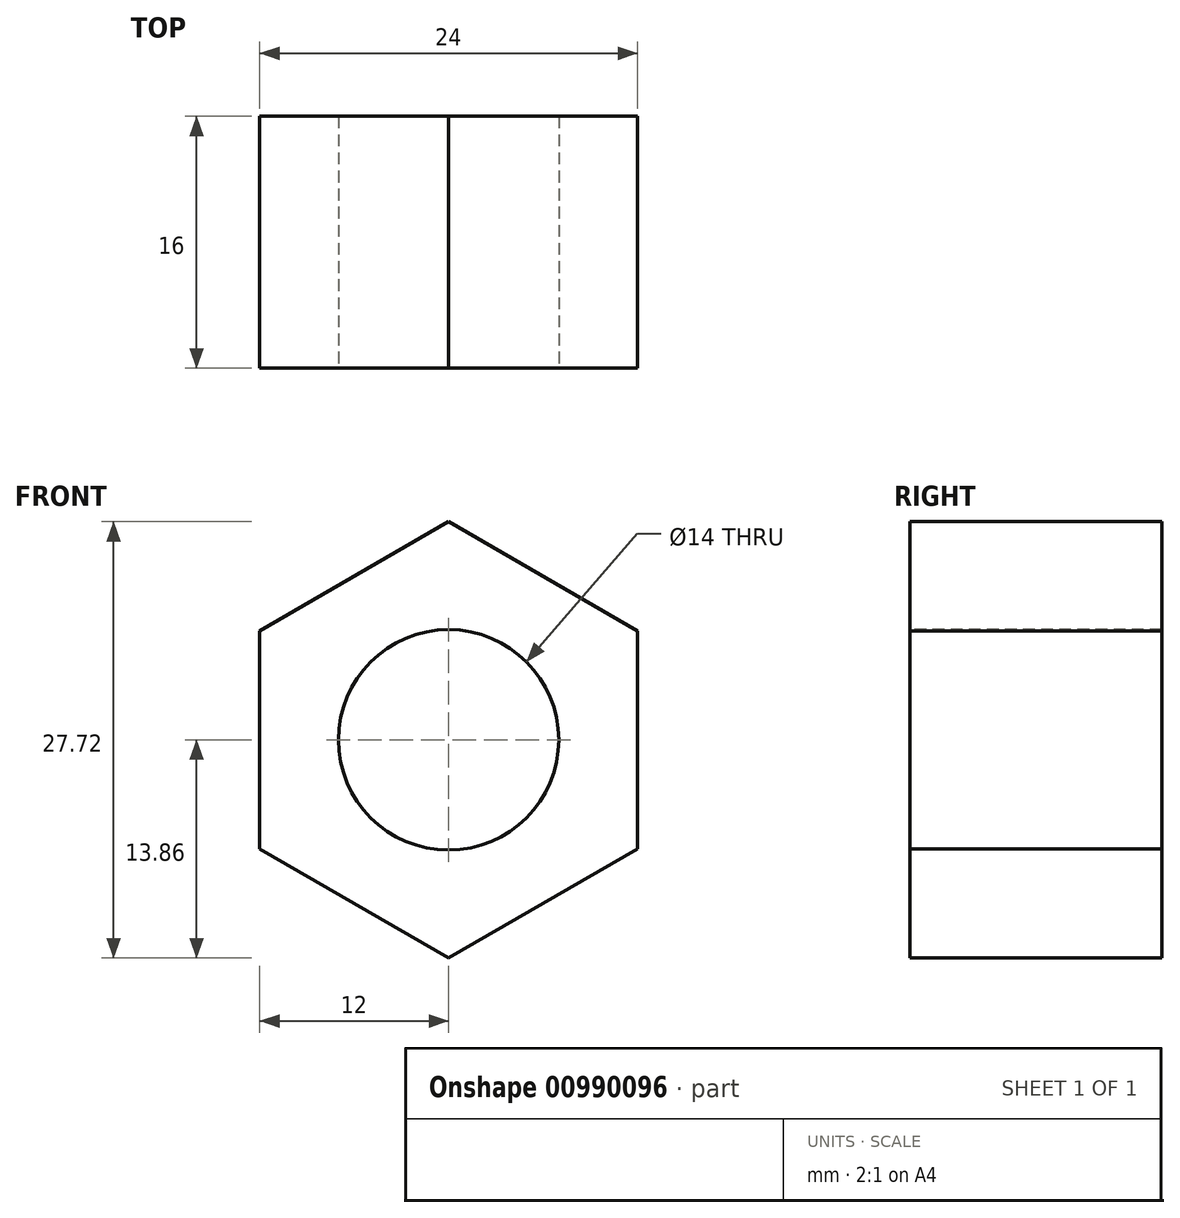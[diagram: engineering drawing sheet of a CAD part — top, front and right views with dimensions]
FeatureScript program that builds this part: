
annotation { "Feature Type Name" : "Feature", "Feature Type Description" : "" }
export const myFeature = defineFeature(function(context is Context, id is Id, definition is map)
    precondition{}
    {
        {
            var Q0;
            Q0=qCreatedBy(makeId("Front.planeOp"),FACE);
            var sketch = newSketch(context, id + "F0", { "sketchPlane" : qUnion([Q0])});
            skCircle(sketch, "E0.cCircle", {"center": v(0, 0) * mm, "radius": 12 * mm, "construction": true});
            skLineSegment(sketch, "E0.0", {"start": v(-12, 6.93) * mm, "end": v(0, 13.86) * mm});
            skLineSegment(sketch, "E0.1", {"start": v(0, 13.86) * mm, "end": v(12, 6.93) * mm});
            skLineSegment(sketch, "E0.2", {"start": v(12, 6.93) * mm, "end": v(12, -6.93) * mm});
            skLineSegment(sketch, "E0.3", {"start": v(12, -6.93) * mm, "end": v(0, -13.86) * mm});
            skLineSegment(sketch, "E0.4", {"start": v(0, -13.86) * mm, "end": v(-12, -6.93) * mm});
            skLineSegment(sketch, "E0.5", {"start": v(-12, -6.93) * mm, "end": v(-12, 6.93) * mm});
            skPoint(sketch, "E0.0.midPoint", {"position": v(-6, 10.4) * mm});
            skSolve(sketch);
        }
        {
            var Q0;
            Q0=makeQuery(id+"F0.imprint","IMPRINT",FACE,{"disambiguationData":[TD([[makeQuery(id+"F0.imprint","IMPRINT",EDGE,{"derivedFrom":sQuery(id+"F0.wireOp",EDGE,"E0.0")}),-1.0]])]});
            extrude(context, id + "F1", {"entities" : qUnion([Q0]), "endBound" : BoundingType.SYMMETRIC, "depth" : 16 * mm, "offsetDistance" : 25 * mm});
        }
        {
            var Q0;
            Q0=makeQuery(id+"F1.opExtrude","CAP_FACE",FACE,{"disambiguationData":[OSD([sQuery(id+"F0.wireOp",EDGE,"E0.0"),sQuery(id+"F0.wireOp",EDGE,"E0.1"),sQuery(id+"F0.wireOp",EDGE,"E0.2"),sQuery(id+"F0.wireOp",EDGE,"E0.3"),sQuery(id+"F0.wireOp",EDGE,"E0.4"),sQuery(id+"F0.wireOp",EDGE,"E0.5")])],"isStart":false});
            var sketch = newSketch(context, id + "F2", { "sketchPlane" : qUnion([Q0])});
            skPoint(sketch, "E1", {"position": v(0, 0) * mm});
            skSolve(sketch);
        }
        {
            var Q0;
            Q0=sQuery(id+"F2.wireOp",VERTEX,"E1");
            var Q1;
            Q1=makeQuery(id+"F1.opExtrude","SWEPT_BODY",BODY,{"disambiguationData":[OSD([sQuery(id+"F0.wireOp",EDGE,"E0.0"),sQuery(id+"F0.wireOp",EDGE,"E0.1"),sQuery(id+"F0.wireOp",EDGE,"E0.2"),sQuery(id+"F0.wireOp",EDGE,"E0.3"),sQuery(id+"F0.wireOp",EDGE,"E0.4"),sQuery(id+"F0.wireOp",EDGE,"E0.5")])]});
            hole(context, id + "F3", {"style" : HoleStyle.SIMPLE, "endStyle" : HoleEndStyle.THROUGH, "standardTappedOrClearance" : lookupTablePath({ "standard" : "ISO", "engagement" : "75%", "pitch" : "2 mm", "size" : "M16", "type" : "Tapped" }), "standardBlindInLast" : lookupTablePath({ "standard" : "ISO", "fit" : "Normal", "engagement" : "75%", "pitch" : "2 mm", "size" : "M16", "type" : "Clearance & tapped" }), "holeDiameter" : 14 * mm, "majorDiameter" : 16 * mm, "showTappedDepth" : true, "isTappedThrough" : true, "tappedDepth" : 12 * mm, "tapClearance" : 3, "locations" : qUnion([Q0]), "scope" : qUnion([Q1])});
        }
    });
